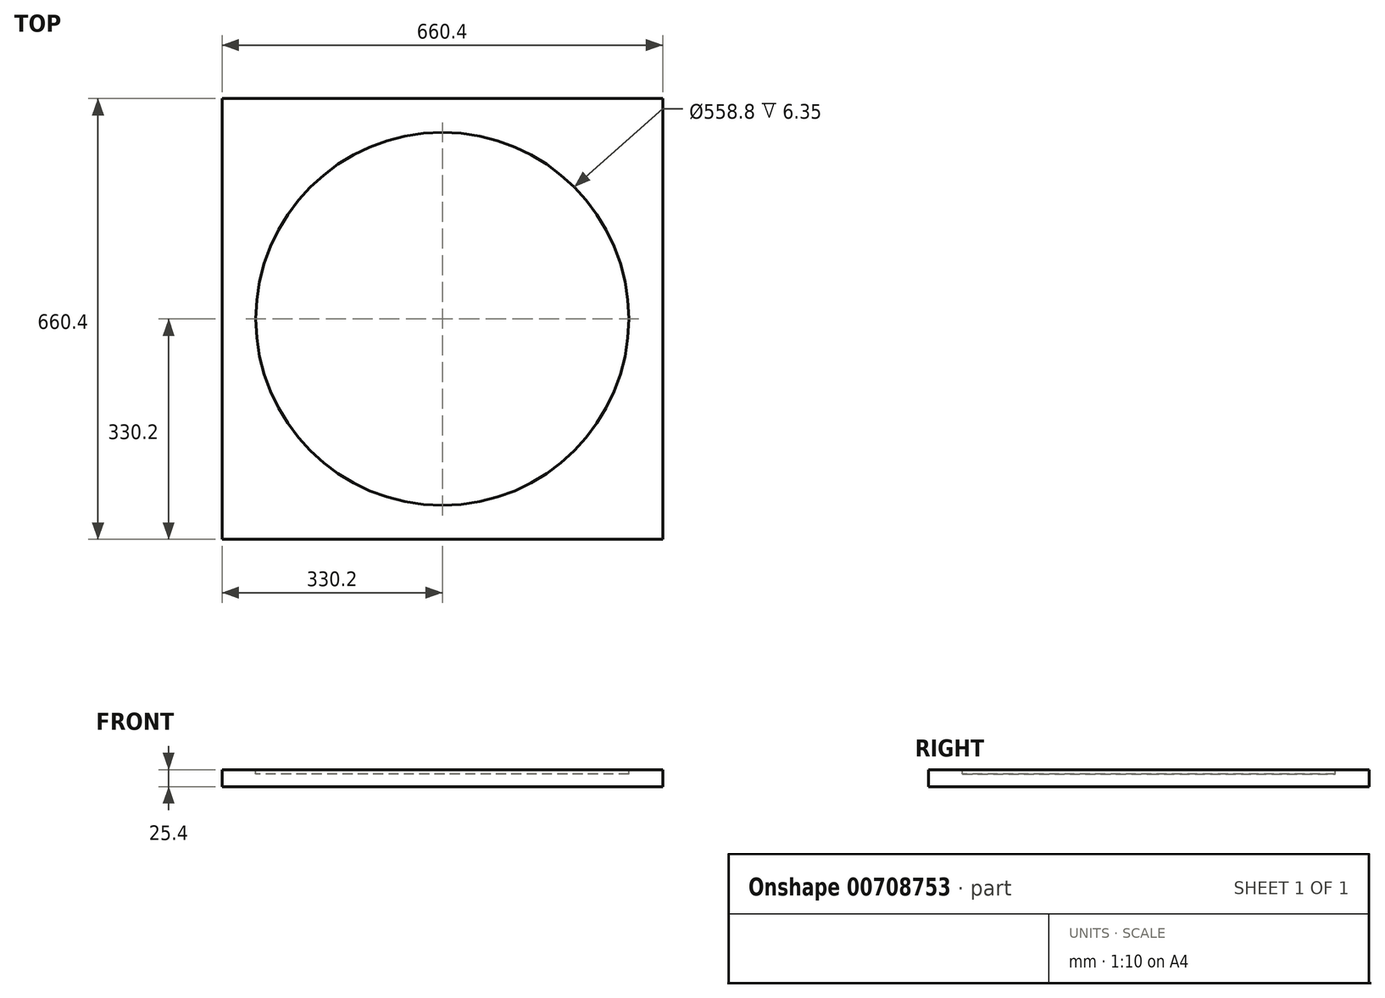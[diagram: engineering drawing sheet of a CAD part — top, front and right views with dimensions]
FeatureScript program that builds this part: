
annotation { "Feature Type Name" : "Feature", "Feature Type Description" : "" }
export const myFeature = defineFeature(function(context is Context, id is Id, definition is map)
    precondition{}
    {
        {
            var Q0;
            Q0=qCreatedBy(makeId("Top.planeOp"),FACE);
            var sketch = newSketch(context, id + "F0", { "sketchPlane" : qUnion([Q0])});
            skLineSegment(sketch, "E0.bottom", {"start": v(0, 0) * mm, "end": v(660.4, 0) * mm});
            skLineSegment(sketch, "E0.top", {"start": v(0, 660.4) * mm, "end": v(660.4, 660.4) * mm});
            skLineSegment(sketch, "E0.left", {"start": v(0, 0) * mm, "end": v(0, 660.4) * mm});
            skLineSegment(sketch, "E0.right", {"start": v(660.4, 0) * mm, "end": v(660.4, 660.4) * mm});
            skLineSegment(sketch, "E1.bottom", {"start": v(660.4, 660.4) * mm, "end": v(-101.6, 660.4) * mm});
            skSolve(sketch);
        }
        {
            var Q0;
            Q0 = qSketchRegion(id + "F0", true);
            extrude(context, id + "F1", {"entities" : qUnion([Q0]), "depth" : 25.4 * mm, "offsetDistance" : 25.4 * mm});
        }
        {
            var Q0;
            Q0=makeQuery(id+"F1.opExtrude","CAP_FACE",FACE,{"disambiguationData":[OSD([sQuery(id+"F0.wireOp",EDGE,"E0.bottom"),sQuery(id+"F0.wireOp",EDGE,"E0.left"),sQuery(id+"F0.wireOp",EDGE,"E0.right"),sQuery(id+"F0.wireOp",EDGE,"E1.bottom")])],"isStart":false});
            var sketch = newSketch(context, id + "F2", { "sketchPlane" : qUnion([Q0])});
            skCircle(sketch, "E2", {"center": v(330.2, 330.2) * mm, "radius": 279.4 * mm});
            skLineSegment(sketch, "E3", {"start": v(0, 330.2) * mm, "end": v(330.2, 330.2) * mm, "construction": true});
            skLineSegment(sketch, "E4", {"start": v(330.2, 330.2) * mm, "end": v(330.2, 0) * mm, "construction": true});
            skSolve(sketch);
        }
        {
            var Q0;
            Q0 = qSketchRegion(id + "F2", true);
            extrude(context, id + "F3", {"entities" : qUnion([Q0]), "operationType" : NewBodyOperationType.REMOVE, "oppositeDirection" : true, "depth" : 6.35 * mm, "offsetDistance" : 25.4 * mm});
        }
    });
